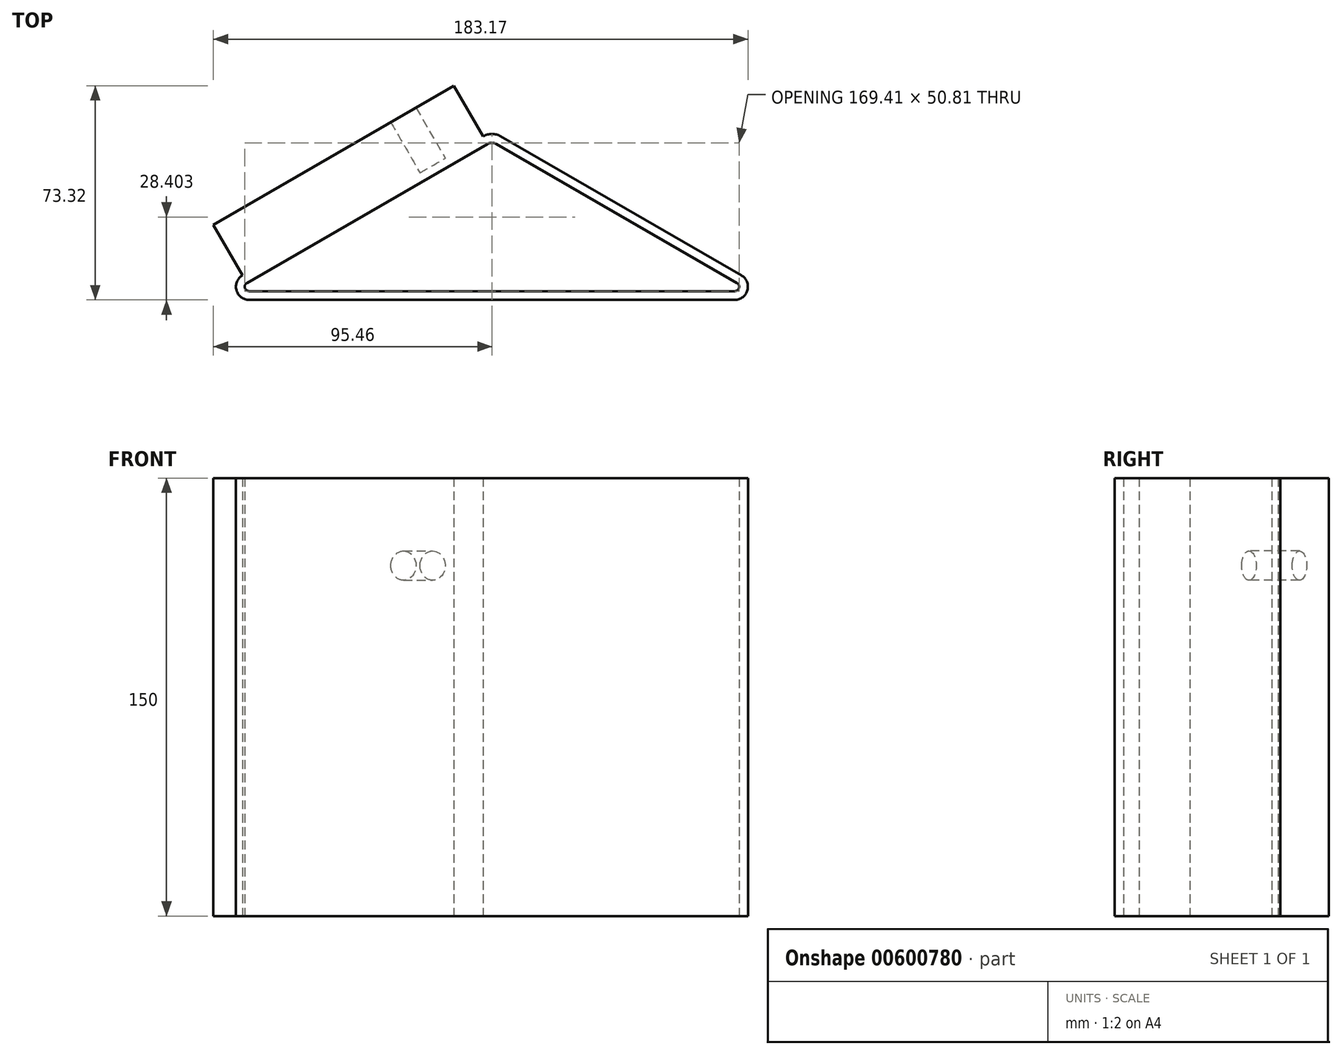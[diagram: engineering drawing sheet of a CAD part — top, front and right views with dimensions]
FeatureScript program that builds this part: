
annotation { "Feature Type Name" : "Feature", "Feature Type Description" : "" }
export const myFeature = defineFeature(function(context is Context, id is Id, definition is map)
    precondition{}
    {
        {
            var Q0;
            Q0=qCreatedBy(makeId("Top.planeOp"),FACE);
            var sketch = newSketch(context, id + "F0", { "sketchPlane" : qUnion([Q0])});
            skLineSegment(sketch, "E0", {"start": v(0, 0) * mm, "end": v(-83.2, 0) * mm});
            skLineSegment(sketch, "E1", {"start": v(0, 0) * mm, "end": v(83.2, 0) * mm});
            skLineSegment(sketch, "E2", {"start": v(85.46, 8.4) * mm, "end": v(3, 56) * mm});
            skLineSegment(sketch, "E3", {"start": v(-3, 56) * mm, "end": v(-85.46, 8.4) * mm});
            skLineSegment(sketch, "E4", {"start": v(0, 57.74) * mm, "end": v(0, 0) * mm, "construction": true});
            skLineSegment(sketch, "E5", {"start": v(47.93, 57.74) * mm, "end": v(-65.55, 57.74) * mm, "construction": true});
            skPoint(sketch, "E6.visualSharp", {"position": v(-100, 0) * mm});
            skArc(sketch, "E6.filletArc", {"start": v(-85.46, 8.4) * mm, "mid": v(-87.55, 3.34) * mm, "end": v(-83.2, 0) * mm});
            skPoint(sketch, "E7.visualSharp", {"position": v(0, 57.74) * mm});
            skArc(sketch, "E7.filletArc", {"start": v(3, 56) * mm, "mid": v(0, 56.8) * mm, "end": v(-3, 56) * mm});
            skPoint(sketch, "E8.visualSharp", {"position": v(100, 0) * mm});
            skArc(sketch, "E8.filletArc", {"start": v(83.2, 0) * mm, "mid": v(87.55, 3.34) * mm, "end": v(85.46, 8.4) * mm});
            skLineSegment(sketch, "E9", {"start": v(0, 3) * mm, "end": v(-83.2, 3) * mm});
            skLineSegment(sketch, "E10", {"start": v(-83.96, 5.8) * mm, "end": v(-1.5, 53.4) * mm});
            skLineSegment(sketch, "E11", {"start": v(1.5, 53.4) * mm, "end": v(83.96, 5.8) * mm});
            skLineSegment(sketch, "E12", {"start": v(83.2, 3) * mm, "end": v(0, 3) * mm});
            skPoint(sketch, "E13.visualSharp", {"position": v(88.8, 3) * mm});
            skArc(sketch, "E13.filletArc", {"start": v(83.2, 3) * mm, "mid": v(84.65, 4.11) * mm, "end": v(83.96, 5.8) * mm});
            skPoint(sketch, "E14.visualSharp", {"position": v(0, 54.27) * mm});
            skArc(sketch, "E14.filletArc", {"start": v(1.5, 53.4) * mm, "mid": v(0, 53.8) * mm, "end": v(-1.5, 53.4) * mm});
            skPoint(sketch, "E15.visualSharp", {"position": v(-88.8, 3) * mm});
            skArc(sketch, "E15.filletArc", {"start": v(-83.96, 5.8) * mm, "mid": v(-84.65, 4.11) * mm, "end": v(-83.2, 3) * mm});
            skSolve(sketch);
        }
        {
            var Q0;
            Q0=makeQuery(id+"F0.imprint","IMPRINT",FACE,{"disambiguationData":[TD([[makeQuery(id+"F0.imprint","IMPRINT",EDGE,{"derivedFrom":sQuery(id+"F0.wireOp",EDGE,"E0")}),-1.0]])]});
            extrude(context, id + "F1", {"entities" : qUnion([Q0]), "depth" : 150 * mm, "offsetDistance" : 25 * mm});
        }
        {
            var Q0;
            Q0=makeQuery(id+"F1.opExtrude","SWEPT_FACE",FACE,{"disambiguationData":[OSD([sQuery(id+"F0.wireOp",EDGE,"E3")])]});
            var sketch = newSketch(context, id + "F2", { "sketchPlane" : qUnion([Q0])});
            skCircle(sketch, "E16", {"center": v(-5.4, 30) * mm, "radius": 5 * mm});
            skLineSegment(sketch, "E17", {"start": v(-25.4, 75) * mm, "end": v(69.8, 75) * mm, "construction": true});
            skCircle(sketch, "E18.MirrorC", {"center": v(-5.4, 120) * mm, "radius": 5 * mm});
            skSolve(sketch);
        }
        {
            var Q0;
            Q0=makeQuery(id+"F2.imprint","IMPRINT",FACE,{"disambiguationData":[TD([[makeQuery(id+"F2.imprint","IMPRINT",EDGE,{"derivedFrom":sQuery(id+"F2.wireOp",EDGE,"E16")}),1.0]])]});
            var Q1;
            Q1=makeQuery(id+"F2.imprint","IMPRINT",FACE,{"disambiguationData":[TD([[makeQuery(id+"F2.imprint","IMPRINT",EDGE,{"derivedFrom":sQuery(id+"F2.wireOp",EDGE,"E18.MirrorC")}),-1.0]])]});
            extrude(context, id + "F3", {"entities" : qUnion([Q0, Q1]), "operationType" : NewBodyOperationType.ADD, "depth" : 20 * mm, "offsetDistance" : 25 * mm});
        }
    });
